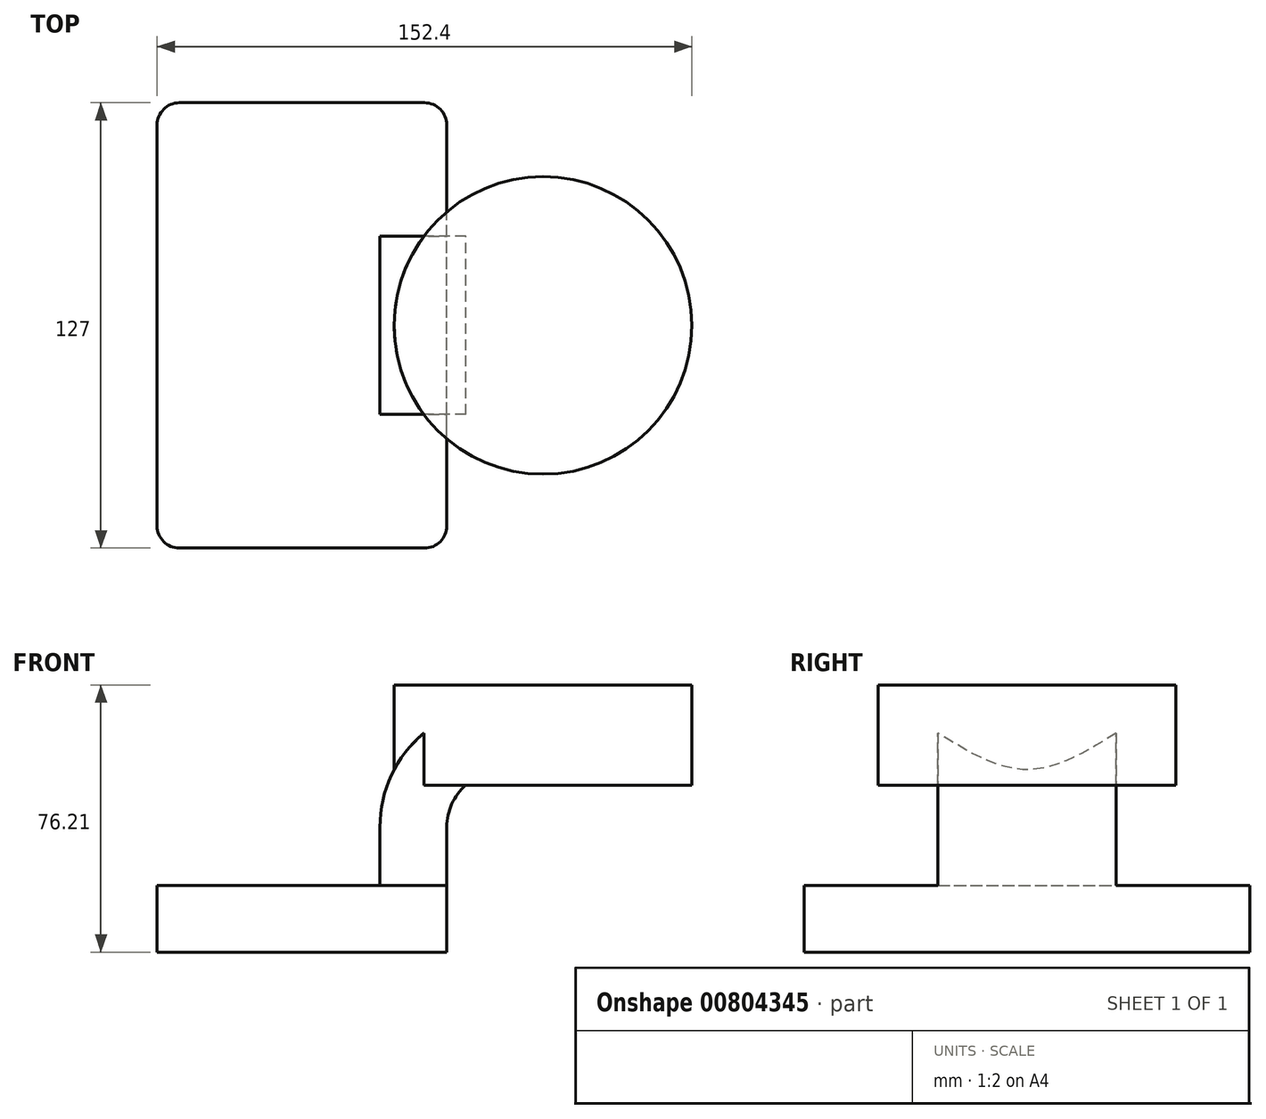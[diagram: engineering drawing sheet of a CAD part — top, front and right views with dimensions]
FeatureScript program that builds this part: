
annotation { "Feature Type Name" : "Feature", "Feature Type Description" : "" }
export const myFeature = defineFeature(function(context is Context, id is Id, definition is map)
    precondition{}
    {
        {
            var Q0;
            Q0=qCreatedBy(makeId("Front.planeOp"),FACE);
            var sketch = newSketch(context, id + "F0", { "sketchPlane" : qUnion([Q0])});
            skLineSegment(sketch, "E0.bottom", {"start": v(-41.28, -9.53) * mm, "end": v(41.28, -9.53) * mm});
            skLineSegment(sketch, "E0.top", {"start": v(-41.28, 9.53) * mm, "end": v(41.28, 9.53) * mm});
            skLineSegment(sketch, "E0.left", {"start": v(-41.28, -9.53) * mm, "end": v(-41.28, 9.53) * mm});
            skLineSegment(sketch, "E0.right", {"start": v(41.28, -9.53) * mm, "end": v(41.28, 9.53) * mm});
            skPoint(sketch, "E0.middle", {"position": v(0, 0) * mm});
            skLineSegment(sketch, "E1.bottom", {"start": v(60.32, 38.1) * mm, "end": v(111.12, 38.1) * mm});
            skLineSegment(sketch, "E1.top", {"start": v(60.32, 66.67) * mm, "end": v(111.12, 66.67) * mm});
            skLineSegment(sketch, "E1.left", {"start": v(60.32, 38.1) * mm, "end": v(60.32, 66.68) * mm});
            skLineSegment(sketch, "E1.right", {"start": v(111.12, 38.1) * mm, "end": v(111.12, 66.68) * mm});
            skPoint(sketch, "E1.middle", {"position": v(85.72, 52.39) * mm});
            skLineSegment(sketch, "E2", {"start": v(41.27, 9.53) * mm, "end": v(41.27, 26.14) * mm});
            skLineSegment(sketch, "E3", {"start": v(52.35, 41.28) * mm, "end": v(68.7, 41.28) * mm});
            skArc(sketch, "E4", {"start": v(41.27, 26.14) * mm, "mid": v(44.34, 35.52) * mm, "end": v(52.35, 41.28) * mm});
            skLineSegment(sketch, "E5.0", {"start": v(50, 60.33) * mm, "end": v(68.7, 60.33) * mm});
            skArc(sketch, "E5.1", {"start": v(22.22, 26.14) * mm, "mid": v(30.04, 48.16) * mm, "end": v(50, 60.33) * mm});
            skLineSegment(sketch, "E5.2", {"start": v(22.22, 9.53) * mm, "end": v(22.22, 26.14) * mm});
            skLineSegment(sketch, "E6", {"start": v(68.7, 66.67) * mm, "end": v(68.7, 38.1) * mm});
            skFitSpline(sketch, "E7", {"points": [v(-41.28, 9.53) * mm, v(60.32, 60.33) * mm], "startDerivative": vector(2.34, 110.4) * mm, "endDerivative": vector(106.23, -8.65) * mm});
            skSolve(sketch);
        }
        {
            var Q0;
            Q0=makeQuery(id+"F0.imprint","IMPRINT",FACE,{"disambiguationData":[TD([[makeQuery(id+"F0.imprint","IMPRINT",EDGE,{"derivedFrom":sQuery(id+"F0.wireOp",EDGE,"E0.bottom")}),1.0]])]});
            extrude(context, id + "F1", {"entities" : qUnion([Q0]), "endBound" : BoundingType.SYMMETRIC, "depth" : 127 * mm, "offsetDistance" : 25.4 * mm});
        }
        {
            var Q0;
            {var subQ4=sQuery(id+"F0.wireOp",EDGE,"E2");Q0=makeQuery(id+"F0.imprint","IMPRINT",FACE,{"disambiguationData":[TD([[makeQuery(id+"F0.imprint","IMPRINT",EDGE,{"derivedFrom":subQ4}),1.0]])]});}
            var Q1;
            {var subQ3=sQuery(id+"F0.wireOp",EDGE,"E3");var subQ5=sQuery(id+"F0.wireOp",EDGE,"E6");var subQ6=makeQuery(id+"F0.imprint","INTERSECT",VERTEX,{"derivedFrom":[subQ3,subQ5]});Q1=makeQuery(id+"F0.imprint","IMPRINT",FACE,{"disambiguationData":[TD([[makeQuery(id+"F0.imprint","IMPRINT",EDGE,{"disambiguationData":[TD([[subQ6,1.0]])],"derivedFrom":subQ3}),1.0]])]});}
            extrude(context, id + "F2", {"entities" : qUnion([Q0, Q1]), "operationType" : NewBodyOperationType.ADD, "endBound" : BoundingType.SYMMETRIC, "depth" : 50.8 * mm, "offsetDistance" : 25.4 * mm});
        }
        {
            var Q0;
            {var subQ1=sQuery(id+"F0.wireOp",EDGE,"E5.1");Q0=makeQuery(id+"F0.imprint","IMPRINT",FACE,{"disambiguationData":[TD([[makeQuery(id+"F0.imprint","IMPRINT",EDGE,{"derivedFrom":subQ1}),1.0]])]});}
            extrude(context, id + "F3", {"entities" : qUnion([Q0]), "operationType" : NewBodyOperationType.ADD, "endBound" : BoundingType.SYMMETRIC, "depth" : 15.88 * mm, "offsetDistance" : 25.4 * mm});
        }
        {
            var Q0;
            {var subQ0=sQuery(id+"F0.wireOp",EDGE,"E1.right");Q0=makeQuery(id+"F0.imprint","IMPRINT",FACE,{"disambiguationData":[TD([[makeQuery(id+"F0.imprint","IMPRINT",EDGE,{"derivedFrom":subQ0}),1.0]])]});}
            var Q1;
            Q1=sQuery(id+"F0.wireOp",EDGE,"E6");
            revolve(context, id + "F4", {"operationType" : NewBodyOperationType.ADD, "surfaceOperationType" : NewSurfaceOperationType.NEW, "entities" : qUnion([Q0]), "axis" : qUnion([Q1]), "revolveType" : RevolveType.FULL});
        }
        {
            var Q0;
            Q0=makeQuery(id+"F1.opExtrude","CAP_EDGE",EDGE,{"disambiguationData":[OSD([sQuery(id+"F0.wireOp",EDGE,"E0.left")])],"isStart":false});
            var Q1;
            Q1=makeQuery(id+"F1.opExtrude","CAP_EDGE",EDGE,{"disambiguationData":[OSD([sQuery(id+"F0.wireOp",EDGE,"E0.right")])],"isStart":false});
            var Q2;
            Q2=makeQuery(id+"F1.opExtrude","CAP_EDGE",EDGE,{"disambiguationData":[OSD([sQuery(id+"F0.wireOp",EDGE,"E0.left")])],"isStart":true});
            var Q3;
            Q3=makeQuery(id+"F1.opExtrude","CAP_EDGE",EDGE,{"disambiguationData":[OSD([sQuery(id+"F0.wireOp",EDGE,"E0.right")])],"isStart":true});
            fillet(context, id + "F5", {"entities" : qUnion([Q0, Q1, Q2, Q3]), "radius" : 6.35 * mm, "tangentPropagation" : true, "allowEdgeOverflow" : false});
        }
    });
